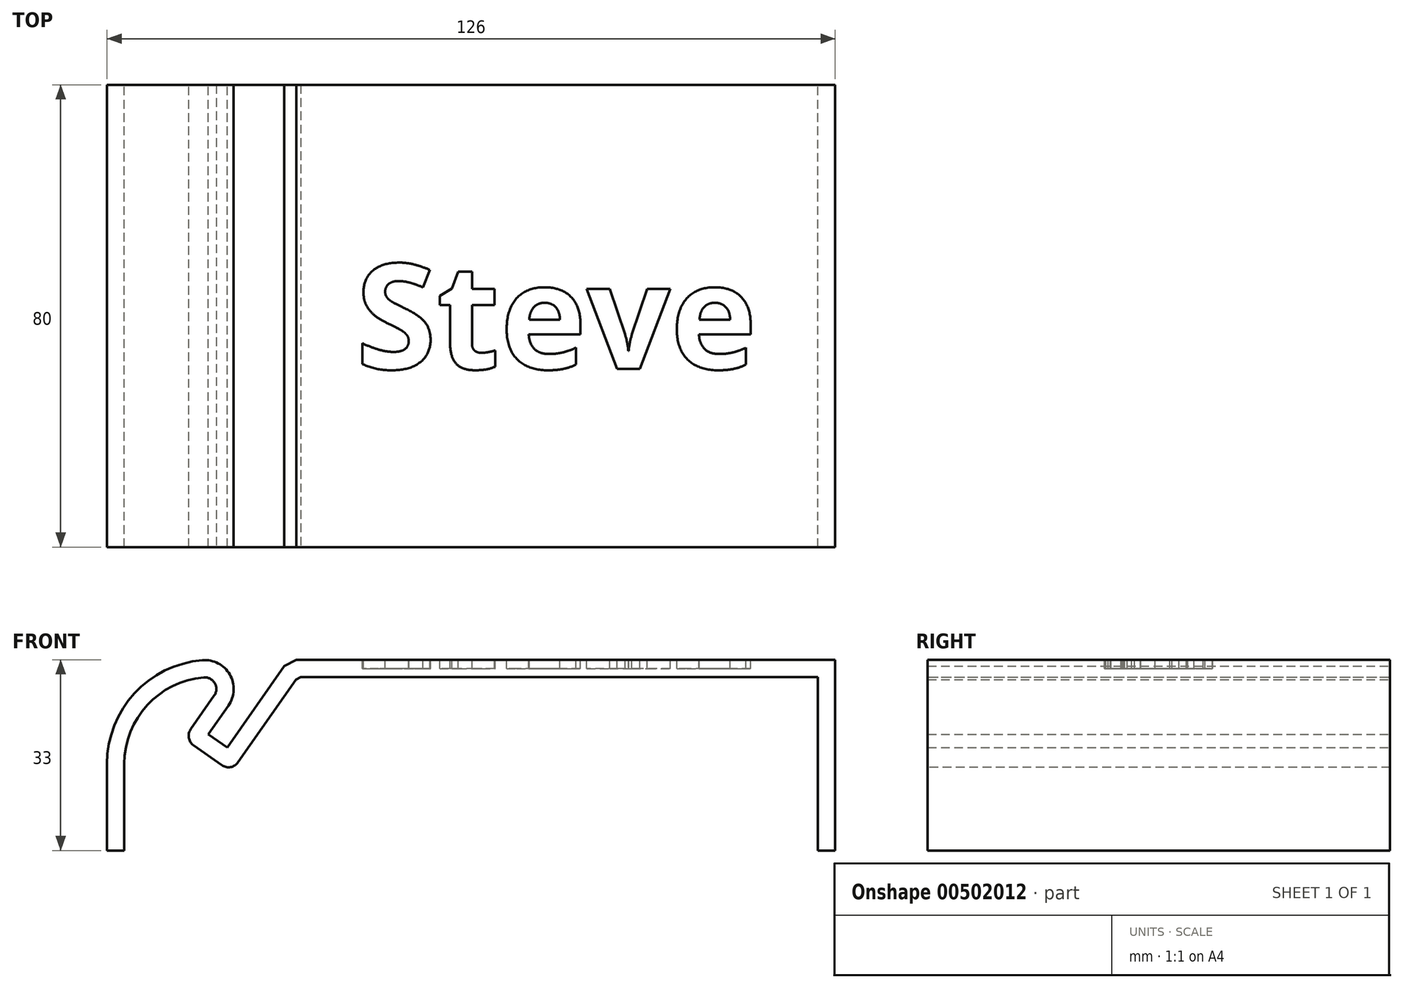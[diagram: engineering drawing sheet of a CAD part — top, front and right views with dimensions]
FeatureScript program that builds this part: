
annotation { "Feature Type Name" : "Feature", "Feature Type Description" : "" }
export const myFeature = defineFeature(function(context is Context, id is Id, definition is map)
    precondition{}
    {
        {
            var Q0;
            Q0=qCreatedBy(makeId("Front.planeOp"),FACE);
            var sketch = newSketch(context, id + "F0", { "sketchPlane" : qUnion([Q0])});
            skLineSegment(sketch, "E0.bottom", {"start": v(60, -15) * mm, "end": v(-60, -15) * mm});
            skLineSegment(sketch, "E0.top", {"start": v(60, 15) * mm, "end": v(-60, 15) * mm});
            skLineSegment(sketch, "E0.left", {"start": v(60, -15) * mm, "end": v(60, 15) * mm});
            skLineSegment(sketch, "E0.right", {"start": v(-60, -15) * mm, "end": v(-60, 15) * mm});
            skPoint(sketch, "E0.middle", {"position": v(0, 0) * mm});
            skSolve(sketch);
        }
        {
            var Q0;
            Q0 = qSketchRegion(id + "F0", true);
            extrude(context, id + "F1", {"entities" : qUnion([Q0]), "depth" : 80 * mm});
        }
        {
            var Q0;
            Q0=makeQuery(id+"F1.opExtrude","CAP_FACE",FACE,{"disambiguationData":[OSD([sQuery(id+"F0.wireOp",EDGE,"E0.bottom"),sQuery(id+"F0.wireOp",EDGE,"E0.top"),sQuery(id+"F0.wireOp",EDGE,"E0.left"),sQuery(id+"F0.wireOp",EDGE,"E0.right")])],"isStart":false});
            var sketch = newSketch(context, id + "F2", { "sketchPlane" : qUnion([Q0])});
            skLineSegment(sketch, "E1.bottom", {"start": v(-38.2, 20.74) * mm, "end": v(-49.66, 4.35) * mm});
            skLineSegment(sketch, "E1.top", {"start": v(-30, 15) * mm, "end": v(-41.47, -1.38) * mm});
            skLineSegment(sketch, "E1.left", {"start": v(-38.2, 20.74) * mm, "end": v(-30, 15) * mm});
            skLineSegment(sketch, "E1.right", {"start": v(-49.66, 4.35) * mm, "end": v(-41.47, -1.38) * mm});
            skSolve(sketch);
        }
        {
            var Q0;
            Q0 = qSketchRegion(id + "F2", true);
            extrude(context, id + "F3", {"entities" : qUnion([Q0]), "operationType" : NewBodyOperationType.REMOVE, "oppositeDirection" : true, "depth" : 80 * mm});
        }
        {
            var Q0;
            Q0=makeQuery(id+"F1.opExtrude","SWEPT_EDGE",EDGE,{"disambiguationData":[OSD([sQuery(id+"F0.wireOp",EDGE,"E0.top"),sQuery(id+"F0.wireOp",EDGE,"E0.right")])]});
            fillet(context, id + "F4", {"entities" : qUnion([Q0]), "radius" : 15 * mm, "tangentPropagation" : true, "allowEdgeOverflow" : false});
        }
        {
            var Q0;
            Q0=makeQuery(id+"F3.boolean.opBoolean","COPY",EDGE,{"derivedFrom":makeQuery(id+"F3.opExtrude","SWEPT_EDGE",EDGE,{"disambiguationData":[OSD([sQuery(id+"F0.wireOp",EDGE,"E0.top"),sQuery(id+"F2.wireOp",EDGE,"E1.top"),sQuery(id+"F2.wireOp",EDGE,"E1.left")])]})});
            chamfer(context, id + "F5", {"entities" : qUnion([Q0]), "width" : 1 * mm, "tangentPropagation" : true});
        }
        {
            var Q0;
            Q0=makeQuery(id+"F3.boolean.opBoolean","INTERSECT",EDGE,{"derivedFrom":[makeQuery(id+"F1.opExtrude","SWEPT_FACE",FACE,{"disambiguationData":[OSD([sQuery(id+"F0.wireOp",EDGE,"E0.top")])]}),makeQuery(id+"F3.opExtrude","SWEPT_FACE",FACE,{"disambiguationData":[OSD([sQuery(id+"F2.wireOp",EDGE,"E1.bottom")])]})]});
            fillet(context, id + "F6", {"entities" : qUnion([Q0]), "radius" : 2 * mm, "tangentPropagation" : true, "allowEdgeOverflow" : false});
        }
        {
            var Q0;
            Q0=makeQuery(id+"F3.boolean.opBoolean","COPY",EDGE,{"derivedFrom":makeQuery(id+"F3.opExtrude","SWEPT_EDGE",EDGE,{"disambiguationData":[OSD([sQuery(id+"F2.wireOp",EDGE,"E1.bottom"),sQuery(id+"F2.wireOp",EDGE,"E1.right")])]})});
            var Q1;
            Q1=makeQuery(id+"F3.boolean.opBoolean","COPY",EDGE,{"derivedFrom":makeQuery(id+"F3.opExtrude","SWEPT_EDGE",EDGE,{"disambiguationData":[OSD([sQuery(id+"F2.wireOp",EDGE,"E1.top"),sQuery(id+"F2.wireOp",EDGE,"E1.right")])]})});
            fillet(context, id + "F7", {"entities" : qUnion([Q0, Q1]), "radius" : 2 * mm, "tangentPropagation" : true, "allowEdgeOverflow" : false});
        }
        {
            var Q0;
            Q0=makeQuery(id+"F1.opExtrude","CAP_FACE",FACE,{"disambiguationData":[OSD([sQuery(id+"F0.wireOp",EDGE,"E0.bottom"),sQuery(id+"F0.wireOp",EDGE,"E0.top"),sQuery(id+"F0.wireOp",EDGE,"E0.left"),sQuery(id+"F0.wireOp",EDGE,"E0.right")])],"isStart":true});
            var Q1;
            Q1=makeQuery(id+"F1.opExtrude","SWEPT_FACE",FACE,{"disambiguationData":[OSD([sQuery(id+"F0.wireOp",EDGE,"E0.bottom")])]});
            var Q2;
            Q2=makeQuery(id+"F1.opExtrude","CAP_FACE",FACE,{"disambiguationData":[OSD([sQuery(id+"F0.wireOp",EDGE,"E0.bottom"),sQuery(id+"F0.wireOp",EDGE,"E0.top"),sQuery(id+"F0.wireOp",EDGE,"E0.left"),sQuery(id+"F0.wireOp",EDGE,"E0.right")])],"isStart":false});
            shell(context, id + "F8", {"entities" : qUnion([Q0, Q1, Q2]), "thickness" : 3 * mm, "oppositeDirection" : true});
        }
        {
            var Q0;
            {var subQ1=sQuery(id+"F0.wireOp",EDGE,"E0.left");var subQ2=sQuery(id+"F0.wireOp",EDGE,"E0.top");Q0=makeQuery(id+"F3.boolean.opBoolean","SPLIT",FACE,{"disambiguationData":[TD([makeQuery(id+"F1.opExtrude","SWEPT_FACE",FACE,{"disambiguationData":[OSD([subQ1])]})])],"derivedFrom":makeQuery(id+"F1.opExtrude","SWEPT_FACE",FACE,{"disambiguationData":[OSD([subQ2])]})});}
            var sketch = newSketch(context, id + "F9", { "sketchPlane" : qUnion([Q0])});
            skText(sketch, "E2", { "text": "Steve", "fontName": "OpenSans-Bold.ttf"});
            skLineSegment(sketch, "E3", {"start": v(18, -30.86) * mm, "end": v(18, 0) * mm, "construction": true});
            skLineSegment(sketch, "E4", {"start": v(18, -49.14) * mm, "end": v(18, -80) * mm, "construction": true});
            const initialGuessF9  = {"E2": [-0.02, -0.04914, 1, 0, 0.01828]};
            skSetInitialGuess(sketch, initialGuessF9);
            skSolve(sketch);
        }
        {
            var Q0;
            Q0 = qSketchRegion(id + "F9", true);
            extrude(context, id + "F10", {"entities" : qUnion([Q0]), "operationType" : NewBodyOperationType.REMOVE, "oppositeDirection" : true, "depth" : 1.5 * mm});
        }
    });
